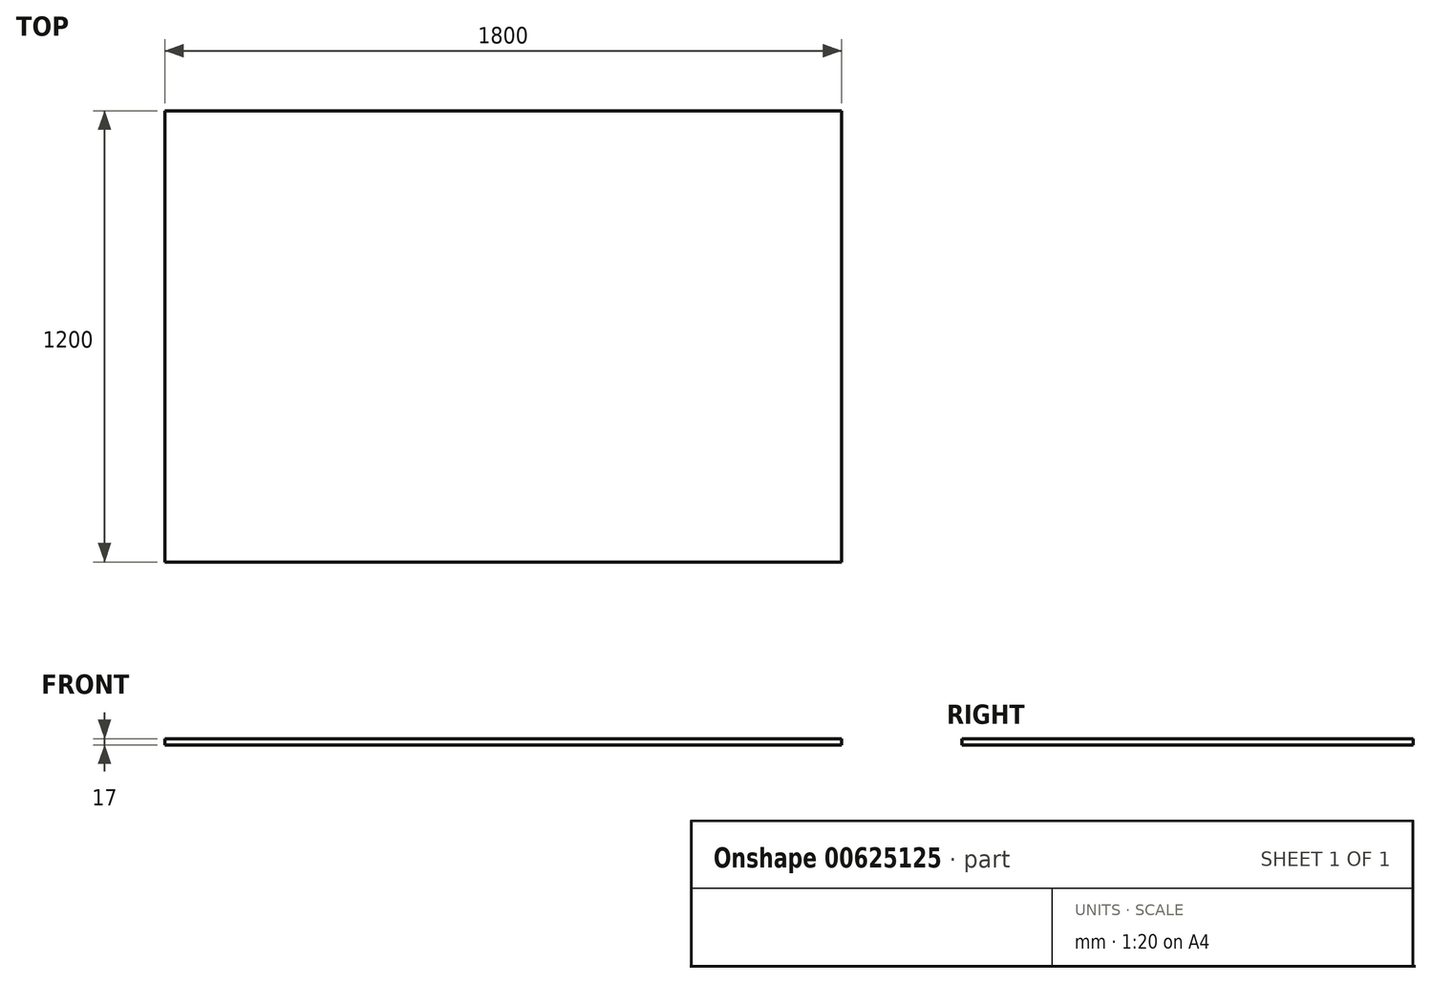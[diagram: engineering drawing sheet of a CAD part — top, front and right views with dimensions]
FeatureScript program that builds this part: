
annotation { "Feature Type Name" : "Feature", "Feature Type Description" : "" }
export const myFeature = defineFeature(function(context is Context, id is Id, definition is map)
    precondition{}
    {
        {
            var Q0;
            Q0=qCreatedBy(makeId("Top.planeOp"),FACE);
            var sketch = newSketch(context, id + "F0", { "sketchPlane" : qUnion([Q0])});
            skLineSegment(sketch, "E0.bottom", {"start": v(-74.92, -74.55) * mm, "end": v(1725.08, -74.55) * mm});
            skLineSegment(sketch, "E0.top", {"start": v(-74.92, 1125.45) * mm, "end": v(1725.08, 1125.45) * mm});
            skLineSegment(sketch, "E0.left", {"start": v(-74.92, -74.55) * mm, "end": v(-74.92, 1125.45) * mm});
            skLineSegment(sketch, "E0.right", {"start": v(1725.08, -74.55) * mm, "end": v(1725.08, 1125.45) * mm});
            skSolve(sketch);
        }
        {
            var Q0;
            Q0 = qSketchRegion(id + "F0", true);
            extrude(context, id + "F1", {"entities" : qUnion([Q0]), "depth" : 17 * mm, "offsetDistance" : 25 * mm});
        }
    });
